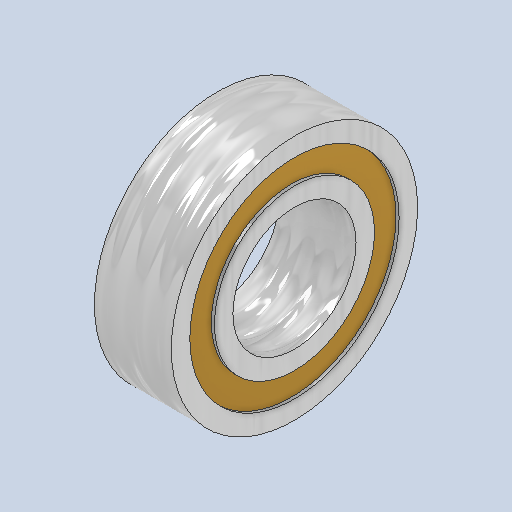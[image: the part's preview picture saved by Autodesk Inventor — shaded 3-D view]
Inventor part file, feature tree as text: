
AUTODESK INVENTOR PART (.ipt)
format: ipt  version: 2024 (Build 280153000, 153)  size: 177,664 bytes
history: native  units: in
note: dims shown in document units (in); Inventor stores cm internally (conversion verified against a paired STEP export)
features: revolve x1
ambient origin geometry x8: Origin, YZ Plane, XZ Plane, XY Plane, X Axis, Y Axis, Z Axis, Center Point
bodies: Solid1 (feature_tree)
feature tree (1):
  revolve  "Revolve1"  [1 undecoded]
note: 1 required parameter value undecoded (feature->parameter linkage not recoverable at this tier; creation-order binding heuristic only, values carry confidence <= 0.55)
